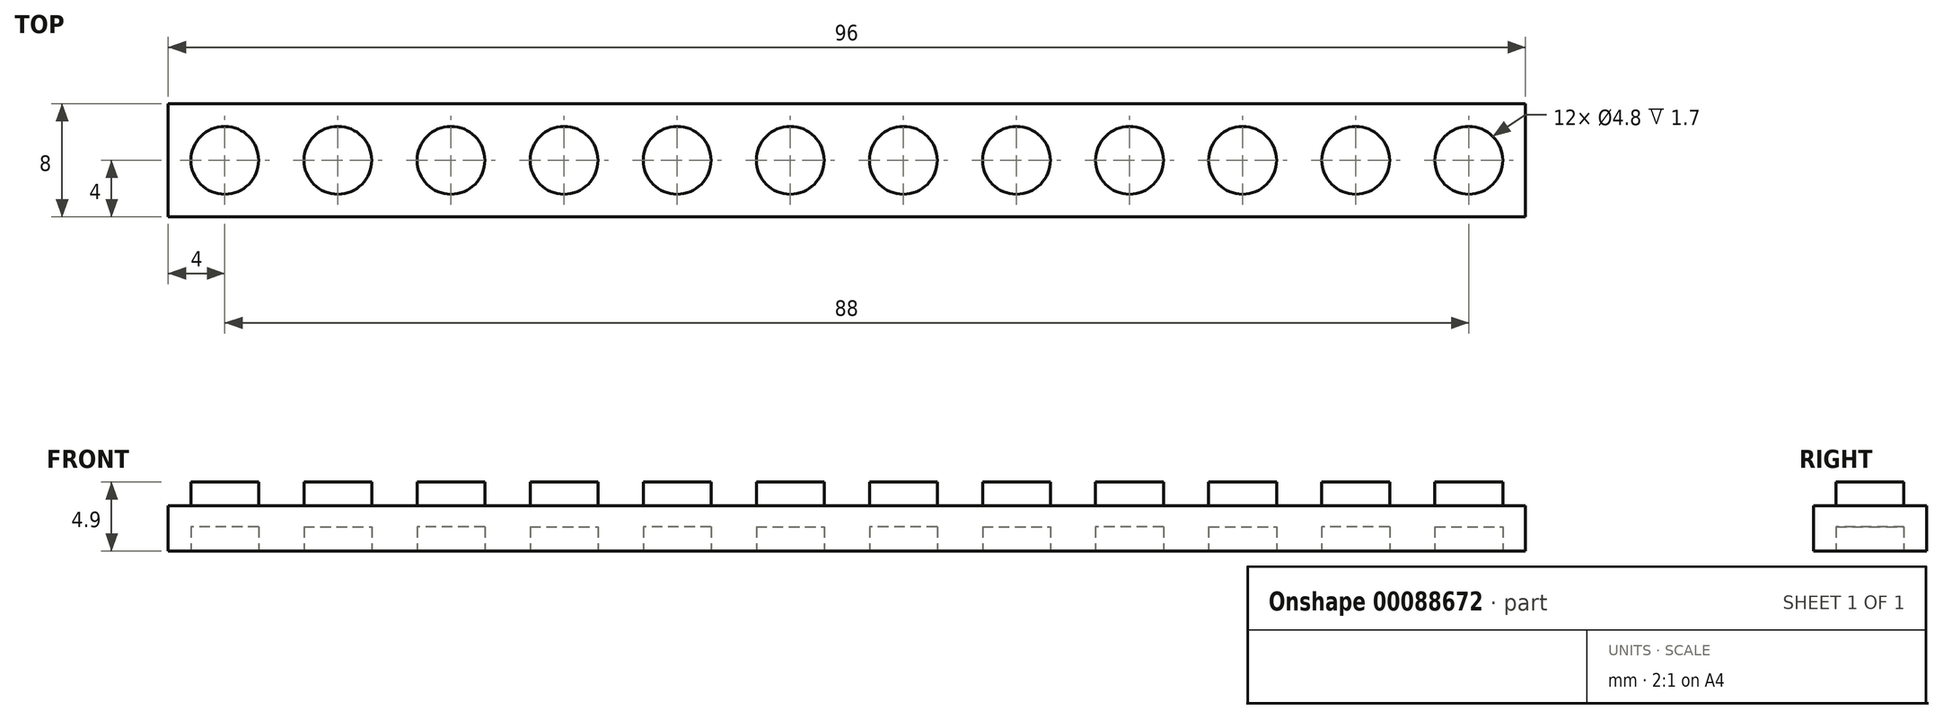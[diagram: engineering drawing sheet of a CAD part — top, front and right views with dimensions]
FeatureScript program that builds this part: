
annotation { "Feature Type Name" : "Feature", "Feature Type Description" : "" }
export const myFeature = defineFeature(function(context is Context, id is Id, definition is map)
    precondition{}
    {
        {
            var Q0;
            Q0=qCreatedBy(makeId("Front.planeOp"),FACE);
            var sketch = newSketch(context, id + "F0", { "sketchPlane" : qUnion([Q0])});
            skLineSegment(sketch, "E0.bottom", {"start": v(-4, 3.2) * mm, "end": v(-2.4, 3.2) * mm});
            skLineSegment(sketch, "E0.top", {"start": v(-4, 0) * mm, "end": v(4, 0) * mm});
            skLineSegment(sketch, "E0.left", {"start": v(-4, 3.2) * mm, "end": v(-4, 0) * mm});
            skLineSegment(sketch, "E0.right", {"start": v(4, 3.2) * mm, "end": v(4, 0) * mm});
            skLineSegment(sketch, "E1.top", {"start": v(-2.4, 4.9) * mm, "end": v(2.4, 4.9) * mm});
            skLineSegment(sketch, "E1.left", {"start": v(-2.4, 3.2) * mm, "end": v(-2.4, 4.9) * mm});
            skLineSegment(sketch, "E1.right", {"start": v(2.4, 3.2) * mm, "end": v(2.4, 4.9) * mm});
            skLineSegment(sketch, "E2", {"start": v(0, 0) * mm, "end": v(0, 24.04) * mm, "construction": true});
            skLineSegment(sketch, "E3.trimOffspring", {"start": v(2.4, 3.2) * mm, "end": v(4, 3.2) * mm});
            skSolve(sketch);
        }
        {
            var Q0;
            Q0=makeQuery(id+"F0.imprint","IMPRINT",FACE,{"disambiguationData":[TD([[makeQuery(id+"F0.imprint","IMPRINT",EDGE,{"derivedFrom":sQuery(id+"F0.wireOp",EDGE,"E0.bottom")}),-1.0]])]});
            extrude(context, id + "F1", {"entities" : qUnion([Q0]), "depth" : 8 * mm});
        }
        {
            var Q0;
            Q0=qCreatedBy(makeId("Top.planeOp"),FACE);
            var Q1;
            Q1=makeQuery(id+"F1.opExtrude","CAP_VERTEX",VERTEX,{"disambiguationData":[OSD([sQuery(id+"F0.wireOp",EDGE,"E1.top"),sQuery(id+"F0.wireOp",EDGE,"E1.right")])],"isStart":true});
            cPlane(context, id + "F2", {"entities" : qUnion([Q0, Q1]), "cplaneType" : CPlaneType.PLANE_POINT, "offset" : 152.4 * mm, "width" : 152.4 * mm, "height" : 152.4 * mm});
        }
        {
            var Q0;
            Q0=qCreatedBy(id+"F2.planeOp",FACE);
            var sketch = newSketch(context, id + "F3", { "sketchPlane" : qUnion([Q0])});
            skLineSegment(sketch, "E4.0", {"start": v(-4, -8) * mm, "end": v(-4, 0) * mm});
            skLineSegment(sketch, "E5.0", {"start": v(4, -8) * mm, "end": v(4, 0) * mm});
            skLineSegment(sketch, "E6", {"start": v(-4, 0) * mm, "end": v(4, 0) * mm});
            skLineSegment(sketch, "E7", {"start": v(-4, -8) * mm, "end": v(4, -8) * mm});
            skLineSegment(sketch, "E8", {"start": v(-4, 0) * mm, "end": v(4, -8) * mm, "construction": true});
            skLineSegment(sketch, "E9", {"start": v(-4, -8) * mm, "end": v(4, 0) * mm, "construction": true});
            skCircle(sketch, "E10", {"center": v(0, -4) * mm, "radius": 2.4 * mm});
            skSolve(sketch);
        }
        {
            var Q0;
            Q0=qSketchRegion(id+"F3",true);
            var Q1;
            Q1=makeQuery(id+"F1.opExtrude","SWEPT_FACE",FACE,{"disambiguationData":[OSD([sQuery(id+"F0.wireOp",EDGE,"E0.bottom")])]});
            extrude(context, id + "F4", {"entities" : qUnion([Q0]), "operationType" : NewBodyOperationType.REMOVE, "endBound" : BoundingType.UP_TO_SURFACE, "oppositeDirection" : true, "endBoundEntityFace" : qUnion([Q1]), "depth" : 25.4 * mm});
        }
        {
            var Q0;
            Q0=qCreatedBy(makeId("Top.planeOp"),FACE);
            var sketch = newSketch(context, id + "F5", { "sketchPlane" : qUnion([Q0])});
            skCircle(sketch, "E11.0", {"center": v(0, -4) * mm, "radius": 2.4 * mm});
            skSolve(sketch);
        }
        {
            var Q0;
            Q0=makeQuery(id+"F5.imprint","IMPRINT",FACE,{"disambiguationData":[TD([[makeQuery(id+"F5.imprint","IMPRINT",EDGE,{"derivedFrom":sQuery(id+"F5.wireOp",EDGE,"E11.0")}),1.0]])]});
            extrude(context, id + "F6", {"entities" : qUnion([Q0]), "operationType" : NewBodyOperationType.REMOVE, "depth" : 1.7 * mm});
        }
        {
            var Q0;
            Q0=qCreatedBy(makeId("Right.planeOp"),FACE);
            var Q1;
            Q1=makeQuery(id+"F1.opExtrude","CAP_VERTEX",VERTEX,{"disambiguationData":[OSD([sQuery(id+"F0.wireOp",EDGE,"E0.right"),sQuery(id+"F0.wireOp",EDGE,"E3.trimOffspring")])],"isStart":false});
            cPlane(context, id + "F7", {"entities" : qUnion([Q0, Q1]), "cplaneType" : CPlaneType.PLANE_POINT, "offset" : 152.4 * mm, "width" : 152.4 * mm, "height" : 152.4 * mm});
        }
        {
            var Q0;
            Q0=makeQuery(id+"F1.opExtrude","SWEPT_BODY",BODY,{"disambiguationData":[OSD([sQuery(id+"F0.wireOp",EDGE,"E0.bottom"),sQuery(id+"F0.wireOp",EDGE,"E0.top"),sQuery(id+"F0.wireOp",EDGE,"E0.left"),sQuery(id+"F0.wireOp",EDGE,"E0.right"),sQuery(id+"F0.wireOp",EDGE,"E1.top"),sQuery(id+"F0.wireOp",EDGE,"E1.left"),sQuery(id+"F0.wireOp",EDGE,"E1.right"),sQuery(id+"F0.wireOp",EDGE,"E3.trimOffspring")])]});
            var Q1;
            Q1=qCreatedBy(id+"F7.planeOp",FACE);
            mirror(context, id + "F8", {"operationType" : NewBodyOperationType.ADD, "entities" : qUnion([Q0]), "mirrorPlane" : qUnion([Q1])});
        }
        {
            var Q0;
            Q0=qCreatedBy(id+"F7.planeOp",FACE);
            var Q1;
            Q1=makeQuery(id+"F8.opPattern","COPY",VERTEX,{"derivedFrom":makeQuery(id+"F1.opExtrude","CAP_VERTEX",VERTEX,{"disambiguationData":[OSD([sQuery(id+"F0.wireOp",EDGE,"E0.bottom"),sQuery(id+"F0.wireOp",EDGE,"E0.left")])],"isStart":false}),"instanceName":"1"});
            cPlane(context, id + "F9", {"entities" : qUnion([Q0, Q1]), "cplaneType" : CPlaneType.PLANE_POINT, "offset" : 152.4 * mm, "width" : 152.4 * mm, "height" : 152.4 * mm});
        }
        {
            var Q0;
            Q0=makeQuery(id+"F1.opExtrude","SWEPT_BODY",BODY,{"disambiguationData":[OSD([sQuery(id+"F0.wireOp",EDGE,"E0.bottom"),sQuery(id+"F0.wireOp",EDGE,"E0.top"),sQuery(id+"F0.wireOp",EDGE,"E0.left"),sQuery(id+"F0.wireOp",EDGE,"E0.right"),sQuery(id+"F0.wireOp",EDGE,"E1.top"),sQuery(id+"F0.wireOp",EDGE,"E1.left"),sQuery(id+"F0.wireOp",EDGE,"E1.right"),sQuery(id+"F0.wireOp",EDGE,"E3.trimOffspring")])]});
            var Q1;
            Q1=qCreatedBy(id+"F9.planeOp",FACE);
            mirror(context, id + "F10", {"operationType" : NewBodyOperationType.ADD, "entities" : qUnion([Q0]), "mirrorPlane" : qUnion([Q1])});
        }
        {
            var Q0;
            Q0=qCreatedBy(makeId("Right.planeOp"),FACE);
            var Q1;
            Q1=makeQuery(id+"F10.opPattern","COPY",VERTEX,{"derivedFrom":makeQuery(id+"F1.opExtrude","CAP_VERTEX",VERTEX,{"disambiguationData":[OSD([sQuery(id+"F0.wireOp",EDGE,"E0.bottom"),sQuery(id+"F0.wireOp",EDGE,"E0.left")])],"isStart":false}),"instanceName":"1"});
            cPlane(context, id + "F11", {"entities" : qUnion([Q0, Q1]), "cplaneType" : CPlaneType.PLANE_POINT, "offset" : 152.4 * mm, "width" : 152.4 * mm, "height" : 152.4 * mm});
        }
        {
            var Q0;
            Q0=makeQuery(id+"F1.opExtrude","SWEPT_BODY",BODY,{"disambiguationData":[OSD([sQuery(id+"F0.wireOp",EDGE,"E0.bottom"),sQuery(id+"F0.wireOp",EDGE,"E0.top"),sQuery(id+"F0.wireOp",EDGE,"E0.left"),sQuery(id+"F0.wireOp",EDGE,"E0.right"),sQuery(id+"F0.wireOp",EDGE,"E1.top"),sQuery(id+"F0.wireOp",EDGE,"E1.left"),sQuery(id+"F0.wireOp",EDGE,"E1.right"),sQuery(id+"F0.wireOp",EDGE,"E3.trimOffspring")])]});
            var Q1;
            Q1=qCreatedBy(id+"F11.planeOp",FACE);
            mirror(context, id + "F12", {"operationType" : NewBodyOperationType.ADD, "entities" : qUnion([Q0]), "mirrorPlane" : qUnion([Q1])});
        }
        {
            var Q0;
            Q0=makeQuery(id+"F1.opExtrude","SWEPT_BODY",BODY,{"disambiguationData":[OSD([sQuery(id+"F0.wireOp",EDGE,"E0.bottom"),sQuery(id+"F0.wireOp",EDGE,"E0.top"),sQuery(id+"F0.wireOp",EDGE,"E0.left"),sQuery(id+"F0.wireOp",EDGE,"E0.right"),sQuery(id+"F0.wireOp",EDGE,"E1.top"),sQuery(id+"F0.wireOp",EDGE,"E1.left"),sQuery(id+"F0.wireOp",EDGE,"E1.right"),sQuery(id+"F0.wireOp",EDGE,"E3.trimOffspring")])]});
            var Q1;
            Q1=makeQuery(id+"F12.opPattern","COPY",FACE,{"derivedFrom":makeQuery(id+"F1.opExtrude","SWEPT_FACE",FACE,{"disambiguationData":[OSD([sQuery(id+"F0.wireOp",EDGE,"E0.left")])]}),"instanceName":"1"});
            mirror(context, id + "F13", {"operationType" : NewBodyOperationType.ADD, "entities" : qUnion([Q0]), "mirrorPlane" : qUnion([Q1])});
        }
        {
            var Q0;
            Q0=makeQuery(id+"F13.opPattern","COPY",FACE,{"derivedFrom":makeQuery(id+"F1.opExtrude","SWEPT_FACE",FACE,{"disambiguationData":[OSD([sQuery(id+"F0.wireOp",EDGE,"E0.left")])]}),"instanceName":"1"});
            var sketch = newSketch(context, id + "F14", { "sketchPlane" : qUnion([Q0])});
            skLineSegment(sketch, "E12.bottom", {"start": v(-15.69, -10.01) * mm, "end": v(15.69, -10.01) * mm});
            skLineSegment(sketch, "E12.top", {"start": v(-15.69, 16.41) * mm, "end": v(15.69, 16.41) * mm});
            skLineSegment(sketch, "E12.left", {"start": v(-15.69, -10.01) * mm, "end": v(-15.69, 16.41) * mm});
            skLineSegment(sketch, "E12.right", {"start": v(15.69, -10.01) * mm, "end": v(15.69, 16.41) * mm});
            skPoint(sketch, "E12.middle", {"position": v(0, 3.2) * mm});
            skSolve(sketch);
        }
        {
            var Q0;
            Q0 = qSketchRegion(id + "F14", true);
            extrude(context, id + "F15", {"entities" : qUnion([Q0]), "operationType" : NewBodyOperationType.REMOVE, "oppositeDirection" : true, "depth" : 4 * 8 * mm, "offsetDistance" : 25.4 * mm});
        }
    });
